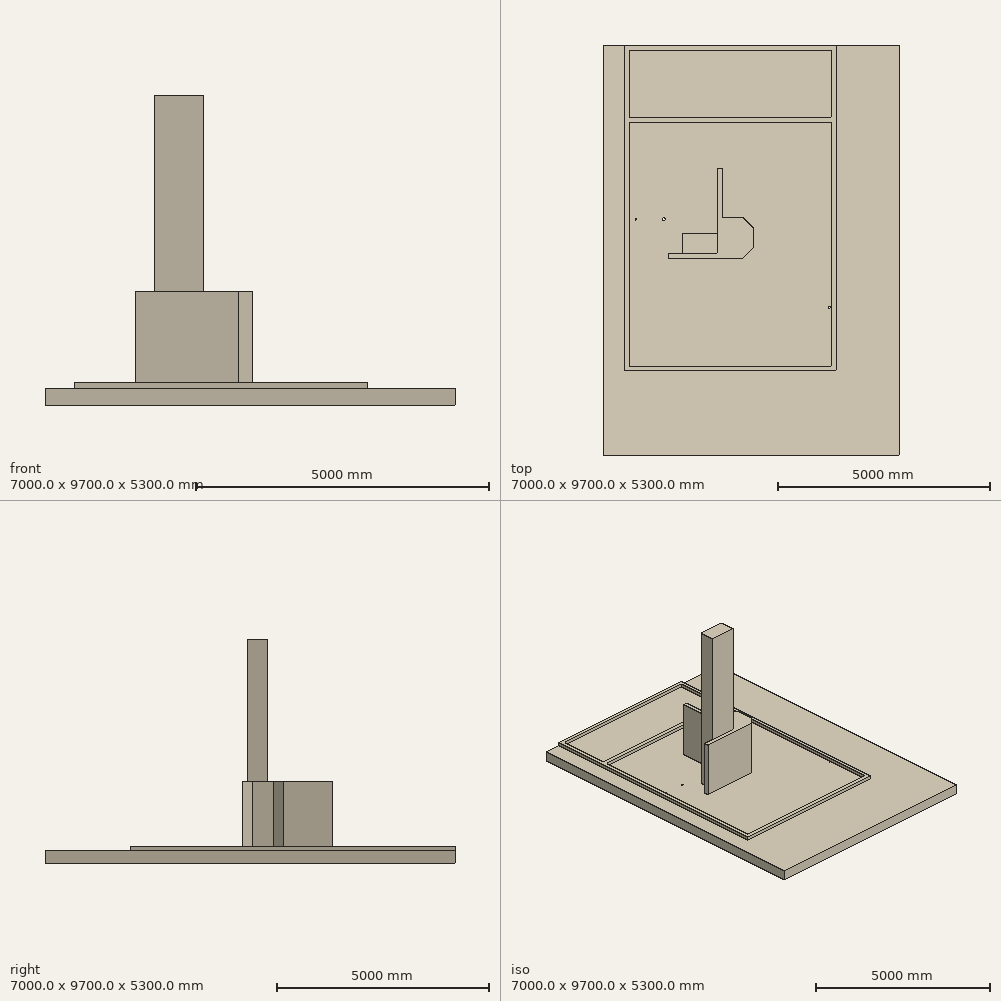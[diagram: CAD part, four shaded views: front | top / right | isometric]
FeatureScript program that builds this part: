
annotation { "Feature Type Name" : "Feature", "Feature Type Description" : "" }
export const myFeature = defineFeature(function(context is Context, id is Id, definition is map)
    precondition{}
    {
        {
            var Q0;
            Q0=qCreatedBy(makeId("Top.planeOp"),FACE);
            var sketch = newSketch(context, id + "F0", { "sketchPlane" : qUnion([Q0])});
            skLineSegment(sketch, "E0.bottom", {"start": v(-5000, 7700) * mm, "end": v(0, 7700) * mm});
            skLineSegment(sketch, "E0.top", {"start": v(-5000, 0) * mm, "end": v(0, 0) * mm});
            skLineSegment(sketch, "E0.left", {"start": v(-5000, 7700) * mm, "end": v(-5000, 0) * mm});
            skLineSegment(sketch, "E0.right", {"start": v(0, 7700) * mm, "end": v(0, 0) * mm});
            skCircle(sketch, "E1", {"center": v(-160, 1500) * mm, "radius": 25 * mm});
            skCircle(sketch, "E2", {"center": v(-4065, 3585) * mm, "radius": 37.5 * mm});
            skCircle(sketch, "E3", {"center": v(-4735, 3585) * mm, "radius": 16 * mm});
            skSolve(sketch);
        }
        {
            var Q0;
            Q0 = qSketchRegion(id + "F0", true);
            extrude(context, id + "F1", {"entities" : qUnion([Q0]), "depth" : 300 * mm, "offsetDistance" : 25 * mm});
        }
        {
            var Q0;
            Q0=makeQuery(id+"F1.opExtrude","CAP_FACE",FACE,{"disambiguationData":[OSD([sQuery(id+"F0.wireOp",EDGE,"E0.bottom"),sQuery(id+"F0.wireOp",EDGE,"E0.top"),sQuery(id+"F0.wireOp",EDGE,"E0.left"),sQuery(id+"F0.wireOp",EDGE,"E0.right"),sQuery(id+"F0.wireOp",EDGE,"E1"),sQuery(id+"F0.wireOp",EDGE,"E2"),sQuery(id+"F0.wireOp",EDGE,"E3")])],"isStart":false});
            var sketch = newSketch(context, id + "F2", { "sketchPlane" : qUnion([Q0])});
            skLineSegment(sketch, "E4", {"start": v(-2680, 2660) * mm, "end": v(-2200, 2660) * mm});
            skLineSegment(sketch, "E5", {"start": v(-2200, 2660) * mm, "end": v(-1959.58, 2900.42) * mm});
            skLineSegment(sketch, "E6", {"start": v(-1959.58, 2900.42) * mm, "end": v(-1959.58, 3390.42) * mm});
            skLineSegment(sketch, "E7", {"start": v(-1959.58, 3390.42) * mm, "end": v(-2200, 3630.83) * mm});
            skLineSegment(sketch, "E8", {"start": v(-2200, 3630.83) * mm, "end": v(-2680, 3630.83) * mm});
            skLineSegment(sketch, "E9", {"start": v(-2680, 3630.83) * mm, "end": v(-2680, 2660) * mm});
            skLineSegment(sketch, "E10", {"start": v(-2680, 2660) * mm, "end": v(-2680, 4800) * mm});
            skLineSegment(sketch, "E11", {"start": v(-2680, 4800) * mm, "end": v(-2810, 4800) * mm});
            skLineSegment(sketch, "E12", {"start": v(-2810, 4800) * mm, "end": v(-2810, 2790) * mm});
            skLineSegment(sketch, "E13", {"start": v(-2810, 2790) * mm, "end": v(-3960, 2790) * mm});
            skLineSegment(sketch, "E14", {"start": v(-3960, 2790) * mm, "end": v(-3960, 2660) * mm});
            skLineSegment(sketch, "E15", {"start": v(-3960, 2660) * mm, "end": v(-2680, 2660) * mm});
            skSolve(sketch);
        }
        {
            var Q0;
            Q0 = qSketchRegion(id + "F2", true);
            extrude(context, id + "F3", {"entities" : qUnion([Q0]), "operationType" : NewBodyOperationType.ADD, "depth" : 1650 * mm, "offsetDistance" : 25 * mm});
        }
        {
            var Q0;
            Q0=makeQuery(id+"F1.opExtrude","CAP_FACE",FACE,{"disambiguationData":[OSD([sQuery(id+"F0.wireOp",EDGE,"E0.bottom"),sQuery(id+"F0.wireOp",EDGE,"E0.top"),sQuery(id+"F0.wireOp",EDGE,"E0.left"),sQuery(id+"F0.wireOp",EDGE,"E0.right"),sQuery(id+"F0.wireOp",EDGE,"E1"),sQuery(id+"F0.wireOp",EDGE,"E2"),sQuery(id+"F0.wireOp",EDGE,"E3")])],"isStart":false});
            var sketch = newSketch(context, id + "F4", { "sketchPlane" : qUnion([Q0])});
            skLineSegment(sketch, "E16.bottom", {"start": v(-5000, 0) * mm, "end": v(0, 0) * mm});
            skLineSegment(sketch, "E16.top", {"start": v(-5000, 6000) * mm, "end": v(0, 6000) * mm});
            skLineSegment(sketch, "E16.left", {"start": v(-5000, 0) * mm, "end": v(-5000, 6000) * mm});
            skLineSegment(sketch, "E16.right", {"start": v(0, 0) * mm, "end": v(0, 6000) * mm});
            skLineSegment(sketch, "E17.0", {"start": v(-4885, 5885) * mm, "end": v(-115, 5885) * mm});
            skLineSegment(sketch, "E17.1", {"start": v(-4885, 115) * mm, "end": v(-4885, 5885) * mm});
            skLineSegment(sketch, "E17.2", {"start": v(-4885, 115) * mm, "end": v(-115, 115) * mm});
            skLineSegment(sketch, "E17.3", {"start": v(-115, 115) * mm, "end": v(-115, 5885) * mm});
            skLineSegment(sketch, "E18", {"start": v(-5000, 6000) * mm, "end": v(-5000, 7700) * mm});
            skLineSegment(sketch, "E19", {"start": v(-5000, 7700) * mm, "end": v(0, 7700) * mm});
            skLineSegment(sketch, "E20", {"start": v(0, 7700) * mm, "end": v(0, 6000) * mm});
            skLineSegment(sketch, "E21", {"start": v(-115, 6000) * mm, "end": v(-115, 7585) * mm});
            skLineSegment(sketch, "E22", {"start": v(-115, 7585) * mm, "end": v(-4885, 7585) * mm});
            skLineSegment(sketch, "E23", {"start": v(-4885, 7585) * mm, "end": v(-4885, 6000) * mm});
            skSolve(sketch);
        }
        {
            var Q0;
            Q0 = qSketchRegion(id + "F4", true);
            extrude(context, id + "F5", {"entities" : qUnion([Q0]), "operationType" : NewBodyOperationType.ADD, "depth" : 100 * mm, "offsetDistance" : 25 * mm});
        }
        {
            var Q0;
            {var subQ0=sQuery(id+"F0.wireOp",EDGE,"E3");var subQ1=sQuery(id+"F0.wireOp",EDGE,"E2");var subQ2=sQuery(id+"F0.wireOp",EDGE,"E1");Q0=makeQuery(id+"F5.boolean.opBoolean","SPLIT",FACE,{"disambiguationData":[TD([makeQuery(id+"F1.opExtrude","SWEPT_FACE",FACE,{"disambiguationData":[OSD([subQ2])]})])],"derivedFrom":makeQuery(id+"F1.opExtrude","CAP_FACE",FACE,{"disambiguationData":[OSD([sQuery(id+"F0.wireOp",EDGE,"E0.bottom"),sQuery(id+"F0.wireOp",EDGE,"E0.top"),sQuery(id+"F0.wireOp",EDGE,"E0.left"),sQuery(id+"F0.wireOp",EDGE,"E0.right"),subQ2,subQ1,subQ0])],"isStart":false})});}
            var sketch = newSketch(context, id + "F6", { "sketchPlane" : qUnion([Q0])});
            skLineSegment(sketch, "E24.bottom", {"start": v(-2810, 2790) * mm, "end": v(-3640, 2790) * mm});
            skLineSegment(sketch, "E24.top", {"start": v(-2810, 3250) * mm, "end": v(-3640, 3250) * mm});
            skLineSegment(sketch, "E24.left", {"start": v(-2810, 2790) * mm, "end": v(-2810, 3250) * mm});
            skLineSegment(sketch, "E24.right", {"start": v(-3640, 2790) * mm, "end": v(-3640, 3250) * mm});
            skSolve(sketch);
        }
        {
            var Q0;
            Q0 = qSketchRegion(id + "F6", true);
            extrude(context, id + "F7", {"entities" : qUnion([Q0]), "operationType" : NewBodyOperationType.ADD, "depth" : 5000 * mm, "offsetDistance" : 25 * mm});
        }
        {
            var Q0;
            Q0=qCreatedBy(makeId("Top.planeOp"),FACE);
            var sketch = newSketch(context, id + "F8", { "sketchPlane" : qUnion([Q0])});
            skLineSegment(sketch, "E25.bottom", {"start": v(-5500, -2000) * mm, "end": v(1500, -2000) * mm});
            skLineSegment(sketch, "E25.top", {"start": v(-5500, 7700) * mm, "end": v(1500, 7700) * mm});
            skLineSegment(sketch, "E25.left", {"start": v(-5500, -2000) * mm, "end": v(-5500, 7700) * mm});
            skLineSegment(sketch, "E25.right", {"start": v(1500, -2000) * mm, "end": v(1500, 7700) * mm});
            skSolve(sketch);
        }
        {
            var Q0;
            Q0 = qSketchRegion(id + "F8", true);
            extrude(context, id + "F9", {"entities" : qUnion([Q0]), "operationType" : NewBodyOperationType.ADD, "depth" : 300 * mm, "offsetDistance" : 25 * mm});
        }
        {
            var Q0;
            {var subQ0=sQuery(id+"F0.wireOp",EDGE,"E3");var subQ1=sQuery(id+"F0.wireOp",EDGE,"E2");var subQ2=sQuery(id+"F0.wireOp",EDGE,"E1");Q0=makeQuery(id+"F9.boolean.opBoolean","MERGE",FACE,{"derivedFrom":[makeQuery(id+"F5.boolean.opBoolean","SPLIT",FACE,{"disambiguationData":[TD([makeQuery(id+"F1.opExtrude","SWEPT_FACE",FACE,{"disambiguationData":[OSD([subQ2])]})])],"derivedFrom":makeQuery(id+"F1.opExtrude","CAP_FACE",FACE,{"disambiguationData":[OSD([sQuery(id+"F0.wireOp",EDGE,"E0.bottom"),sQuery(id+"F0.wireOp",EDGE,"E0.top"),sQuery(id+"F0.wireOp",EDGE,"E0.left"),sQuery(id+"F0.wireOp",EDGE,"E0.right"),subQ2,subQ1,subQ0])],"isStart":false})}),makeQuery(id+"F9.opExtrude","CAP_FACE",FACE,{"disambiguationData":[OSD([sQuery(id+"F8.wireOp",EDGE,"E25.bottom"),sQuery(id+"F8.wireOp",EDGE,"E25.top"),sQuery(id+"F8.wireOp",EDGE,"E25.left"),sQuery(id+"F8.wireOp",EDGE,"E25.right")])],"isStart":false})]});}
            var sketch = newSketch(context, id + "F10", { "sketchPlane" : qUnion([Q0])});
            skCircle(sketch, "E26", {"center": v(-160, 1500) * mm, "radius": 25 * mm});
            skCircle(sketch, "E27", {"center": v(-4065, 3585) * mm, "radius": 37.5 * mm});
            skCircle(sketch, "E28", {"center": v(-4735, 3585) * mm, "radius": 16 * mm});
            skSolve(sketch);
        }
        {
            var Q0;
            Q0 = qSketchRegion(id + "F10", true);
            extrude(context, id + "F11", {"entities" : qUnion([Q0]), "operationType" : NewBodyOperationType.REMOVE, "oppositeDirection" : true, "depth" : 400 * mm, "offsetDistance" : 25 * mm});
        }
    });
